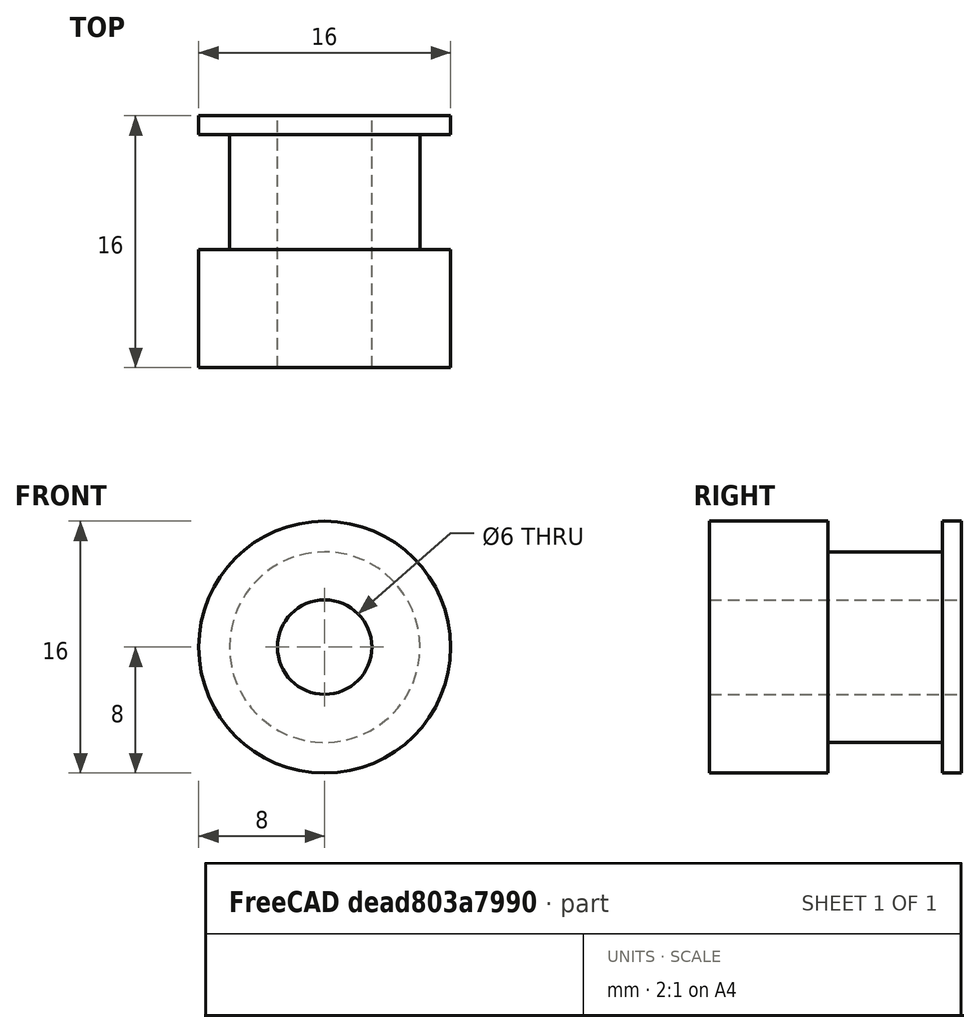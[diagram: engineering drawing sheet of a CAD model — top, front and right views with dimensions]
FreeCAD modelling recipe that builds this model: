
FCSTD DOCUMENT  (FreeCAD 0.17R12560 (Git))
Label: timing_pulley_gt2_20T_bore_6
License: All rights reserved
LicenseURL: http://en.wikipedia.org/wiki/All_rights_reserved
objects: Sketcher::SketchObject×1, PartDesign::Revolution×1
note: 3 computed .brp shape members not serialized (recipe doc carries the construction recipe); baked Part::Feature solids carry a one-line shape summary decoded from their .brp

FEATURE [Sketcher::SketchObject] Sketch
  MapMode = 5
  sketch-geometry (9):
    g0: LineSegment StartX=3 StartY=0 StartZ=0 EndX=3 EndY=16 EndZ=0
    g1: LineSegment StartX=3 StartY=16 StartZ=0 EndX=8 EndY=16 EndZ=0
    g2: LineSegment StartX=8 StartY=7.5 StartZ=0 EndX=8 EndY=0 EndZ=0
    g3: LineSegment StartX=8 StartY=0 StartZ=0 EndX=3 EndY=0 EndZ=0
    g4: LineSegment StartX=8 StartY=7.5 StartZ=0 EndX=6.05 EndY=7.5 EndZ=0
    g5: LineSegment StartX=6.05 StartY=7.5 StartZ=0 EndX=6.05 EndY=14.8 EndZ=0
    g6: LineSegment StartX=6.05 StartY=14.8 StartZ=0 EndX=8 EndY=14.8 EndZ=0
    g7: LineSegment StartX=8 StartY=14.8 StartZ=0 EndX=8 EndY=16 EndZ=0
    g8: LineSegment [constr] StartX=8 StartY=7.5 StartZ=0 EndX=8 EndY=14.8 EndZ=0
  constraints (26):
    c: Vertical(g0)
    c: Coincident(g0,g1)
    c: Horizontal(g1)
    c: Vertical(g2)
    c: Coincident(g2,g3)
    c: Coincident(g3,g0)
    c: Horizontal(g3)
    c: DistanceY(g0,g0) = 16
    c: PointOnObject(g0,g-1)
    c: DistanceX(g-1,g2) = 8
    c: DistanceX(g-1,g0) = 3
    c: DistanceY(g2) = -7.5
    c: Horizontal(g4)
    c: Coincident(g4,g5)
    c: Vertical(g5)
    c: Coincident(g5,g6)
    c: Horizontal(g6)
    c: Coincident(g6,g7)
    c: Coincident(g7,g1)
    c: Vertical(g7)
    c: Coincident(g8,g6)
    c: Vertical(g8)
    c: Coincident(g4,g8)
    c: Coincident(g4,g2)
    c: DistanceY(g8) = 7.3
    c: DistanceX(g-1,g5) = 6.05
FEATURE [PartDesign::Revolution] Revolution
  Angle = 360
  Axis = (0,1,0)
  Base = (0,0,0)
  Profile = -> Sketch
  ReferenceAxis = -> Sketch [V_Axis]
  Reversed = true
